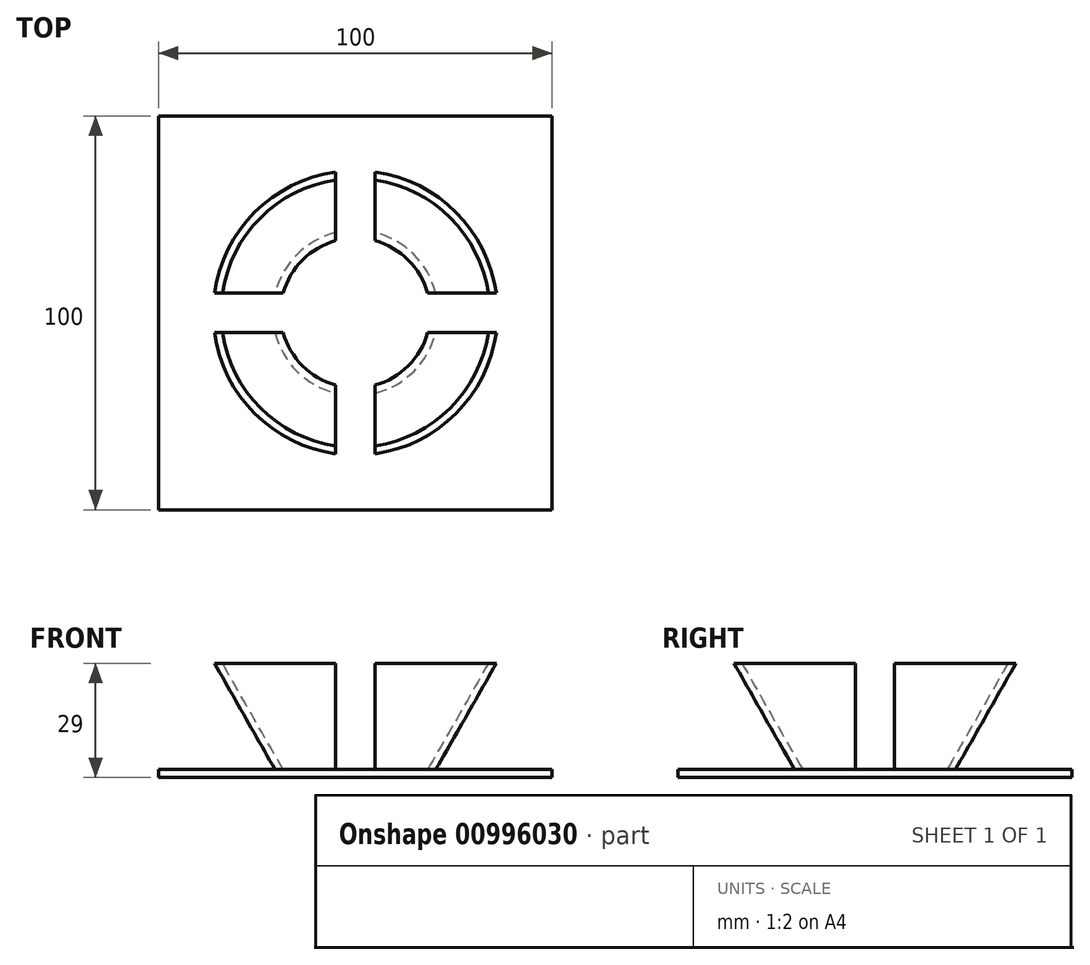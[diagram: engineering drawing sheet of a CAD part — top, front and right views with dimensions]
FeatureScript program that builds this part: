
annotation { "Feature Type Name" : "Feature", "Feature Type Description" : "" }
export const myFeature = defineFeature(function(context is Context, id is Id, definition is map)
    precondition{}
    {
        {
            var Q0;
            Q0=qCreatedBy(makeId("Front.planeOp"),FACE);
            var sketch = newSketch(context, id + "F0", { "sketchPlane" : qUnion([Q0])});
            skLineSegment(sketch, "E0", {"start": v(0, 0) * mm, "end": v(0, 2) * mm});
            skLineSegment(sketch, "E1", {"start": v(0, 2) * mm, "end": v(19, 2) * mm});
            skLineSegment(sketch, "E2", {"start": v(19, 2) * mm, "end": v(34.15, 29) * mm});
            skLineSegment(sketch, "E3", {"start": v(34.15, 29) * mm, "end": v(36.15, 29) * mm});
            skLineSegment(sketch, "E4", {"start": v(36.15, 29) * mm, "end": v(19.88, 0) * mm});
            skLineSegment(sketch, "E5", {"start": v(19.88, 0) * mm, "end": v(0, 0) * mm});
            skLineSegment(sketch, "E6", {"start": v(19, 2) * mm, "end": v(19, 29) * mm});
            skLineSegment(sketch, "E7", {"start": v(19, 29) * mm, "end": v(34.15, 29) * mm});
            skSolve(sketch);
        }
        {
            var Q0;
            Q0=qCreatedBy(makeId("Front.planeOp"),FACE);
            var sketch = newSketch(context, id + "F1", { "sketchPlane" : qUnion([Q0])});
            skLineSegment(sketch, "E8", {"start": v(0, 0) * mm, "end": v(0, 21.8) * mm});
            skSolve(sketch);
        }
        {
            var Q0;
            Q0=makeQuery(id+"F0.imprint","IMPRINT",FACE,{"disambiguationData":[TD([[makeQuery(id+"F0.imprint","IMPRINT",EDGE,{"derivedFrom":sQuery(id+"F0.wireOp",EDGE,"E0")}),-1.0]])]});
            var Q1;
            Q1=sQuery(id+"F1.wireOp",EDGE,"E8");
            revolve(context, id + "F2", {"surfaceOperationType" : NewSurfaceOperationType.NEW, "entities" : qUnion([Q0]), "axis" : qUnion([Q1]), "revolveType" : RevolveType.FULL});
        }
        {
            var Q0;
            Q0=qCreatedBy(makeId("Top.planeOp"),FACE);
            var sketch = newSketch(context, id + "F3", { "sketchPlane" : qUnion([Q0])});
            skLineSegment(sketch, "E9", {"start": v(-72, 0) * mm, "end": v(-72, 5) * mm});
            skLineSegment(sketch, "E10", {"start": v(-72, 5) * mm, "end": v(-5, 5) * mm});
            skLineSegment(sketch, "E11", {"start": v(-5, 5) * mm, "end": v(-5, 72) * mm});
            skLineSegment(sketch, "E12", {"start": v(-5, 72) * mm, "end": v(0, 72) * mm});
            skLineSegment(sketch, "E13", {"start": v(0, 72) * mm, "end": v(5, 72) * mm});
            skLineSegment(sketch, "E14", {"start": v(5, 72) * mm, "end": v(5, 5) * mm});
            skLineSegment(sketch, "E15", {"start": v(5, 5) * mm, "end": v(72, 5) * mm});
            skLineSegment(sketch, "E16", {"start": v(72, 5) * mm, "end": v(72, 0) * mm});
            skLineSegment(sketch, "E17", {"start": v(72, 0) * mm, "end": v(72, -5) * mm});
            skLineSegment(sketch, "E18", {"start": v(72, -5) * mm, "end": v(5, -5) * mm});
            skLineSegment(sketch, "E19", {"start": v(5, -5) * mm, "end": v(5, -72) * mm});
            skLineSegment(sketch, "E20", {"start": v(5, -72) * mm, "end": v(0, -72) * mm});
            skLineSegment(sketch, "E21", {"start": v(0, -72) * mm, "end": v(-5, -72) * mm});
            skLineSegment(sketch, "E22", {"start": v(-5, -72) * mm, "end": v(-5, -5) * mm});
            skLineSegment(sketch, "E23", {"start": v(-5, -5) * mm, "end": v(-72, -5) * mm});
            skLineSegment(sketch, "E24", {"start": v(-72, -5) * mm, "end": v(-72, 0) * mm});
            skSolve(sketch);
        }
        {
            var Q0;
            Q0 = qSketchRegion(id + "F3", true);
            extrude(context, id + "F4", {"entities" : qUnion([Q0]), "operationType" : NewBodyOperationType.REMOVE, "depth" : 30 * mm, "offsetDistance" : 25 * mm, "hasSecondDirection" : true, "secondDirectionOppositeDirection" : true, "secondDirectionDepth" : -2 * mm});
        }
        {
            var Q0;
            Q0=qCreatedBy(makeId("Top.planeOp"),FACE);
            var sketch = newSketch(context, id + "F5", { "sketchPlane" : qUnion([Q0])});
            skLineSegment(sketch, "E25.bottom", {"start": v(50, 50) * mm, "end": v(-50, 50) * mm});
            skLineSegment(sketch, "E25.top", {"start": v(50, -50) * mm, "end": v(-50, -50) * mm});
            skLineSegment(sketch, "E25.left", {"start": v(50, 50) * mm, "end": v(50, -50) * mm});
            skLineSegment(sketch, "E25.right", {"start": v(-50, 50) * mm, "end": v(-50, -50) * mm});
            skPoint(sketch, "E25.middle", {"position": v(0, 0) * mm});
            skSolve(sketch);
        }
        {
            var Q0;
            Q0=makeQuery(id+"F5.imprint","IMPRINT",FACE,{"disambiguationData":[TD([[makeQuery(id+"F5.imprint","IMPRINT",EDGE,{"derivedFrom":sQuery(id+"F5.wireOp",EDGE,"E25.bottom")}),1.0]])]});
            extrude(context, id + "F6", {"entities" : qUnion([Q0]), "operationType" : NewBodyOperationType.ADD, "depth" : 2 * mm, "offsetDistance" : 25 * mm});
        }
    });
